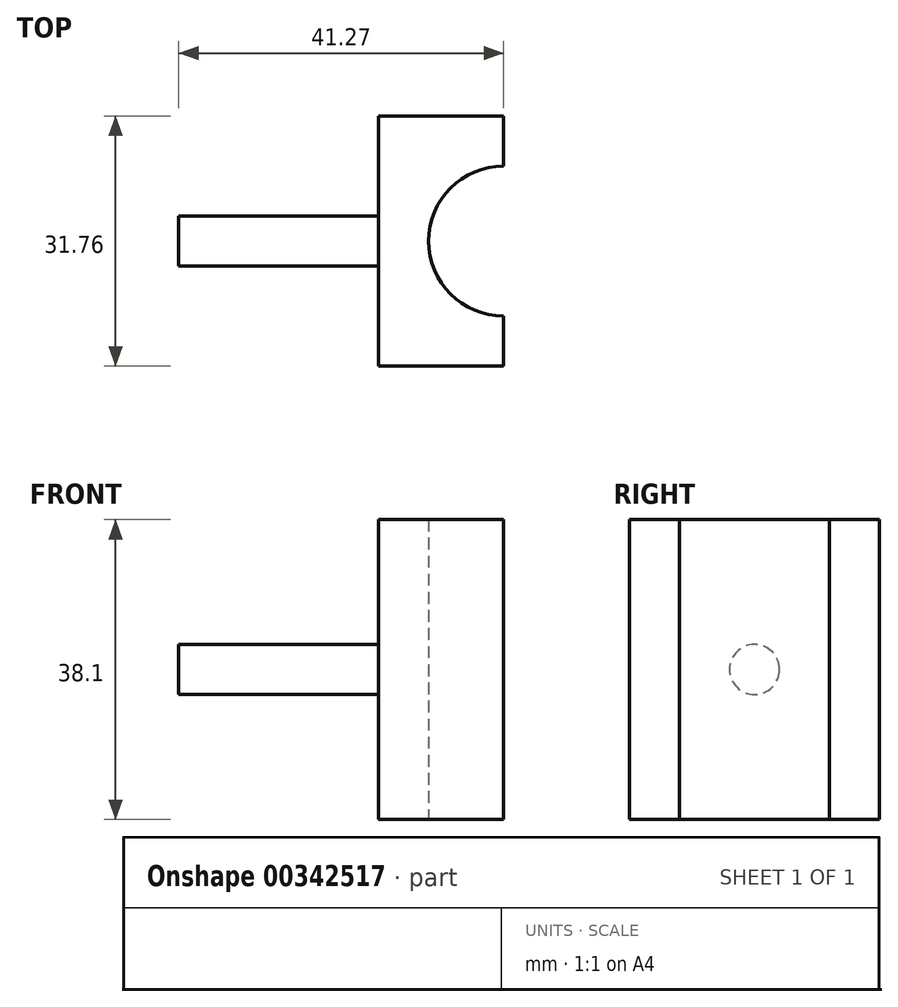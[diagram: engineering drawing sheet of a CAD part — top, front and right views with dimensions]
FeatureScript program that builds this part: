
annotation { "Feature Type Name" : "Feature", "Feature Type Description" : "" }
export const myFeature = defineFeature(function(context is Context, id is Id, definition is map)
    precondition{}
    {
        {
            var Q0;
            Q0=qCreatedBy(makeId("Top.planeOp"),FACE);
            var sketch = newSketch(context, id + "F0", { "sketchPlane" : qUnion([Q0])});
            skLineSegment(sketch, "E0.bottom", {"start": v(-21.5, 15.88) * mm, "end": v(-5.62, 15.88) * mm});
            skLineSegment(sketch, "E0.top", {"start": v(-21.5, -15.88) * mm, "end": v(-5.62, -15.87) * mm});
            skLineSegment(sketch, "E0.left", {"start": v(-21.5, 15.88) * mm, "end": v(-21.5, -15.88) * mm});
            skLineSegment(sketch, "E0.right", {"start": v(-5.62, 15.88) * mm, "end": v(-5.62, -15.87) * mm});
            skPoint(sketch, "E0.middle", {"position": v(-13.55, 0) * mm});
            skArc(sketch, "E1", {"start": v(-5.62, 9.53) * mm, "mid": v(-15.14, 0) * mm, "end": v(-5.62, -9.52) * mm});
            skSolve(sketch);
        }
        {
            var Q0;
            {var subQ1=sQuery(id+"F0.wireOp",EDGE,"E0.bottom");Q0=makeQuery(id+"F0.imprint","IMPRINT",FACE,{"disambiguationData":[TD([[makeQuery(id+"F0.imprint","IMPRINT",EDGE,{"derivedFrom":subQ1}),-1.0]])]});}
            extrude(context, id + "F1", {"entities" : qUnion([Q0]), "depth" : 38.1 * mm});
        }
        {
            var Q0;
            Q0=makeQuery(id+"F1.opExtrude","SWEPT_FACE",FACE,{"disambiguationData":[OSD([sQuery(id+"F0.wireOp",EDGE,"E0.left")])]});
            var sketch = newSketch(context, id + "F2", { "sketchPlane" : qUnion([Q0])});
            skPoint(sketch, "E2", {"position": v(0, 19.05) * mm});
            skPoint(sketch, "E2.positionSnap0", {"position": v(0, 38.1) * mm});
            skCircle(sketch, "E3", {"center": v(0, 19.05) * mm, "radius": 3.18 * mm});
            skSolve(sketch);
        }
        {
            var Q0;
            Q0=makeQuery(id+"F2.imprint","IMPRINT",FACE,{"disambiguationData":[TD([[makeQuery(id+"F2.imprint","IMPRINT",EDGE,{"derivedFrom":sQuery(id+"F2.wireOp",EDGE,"E3")}),1.0]])]});
            extrude(context, id + "F3", {"entities" : qUnion([Q0]), "operationType" : NewBodyOperationType.ADD, "depth" : 25.4 * mm});
        }
    });
